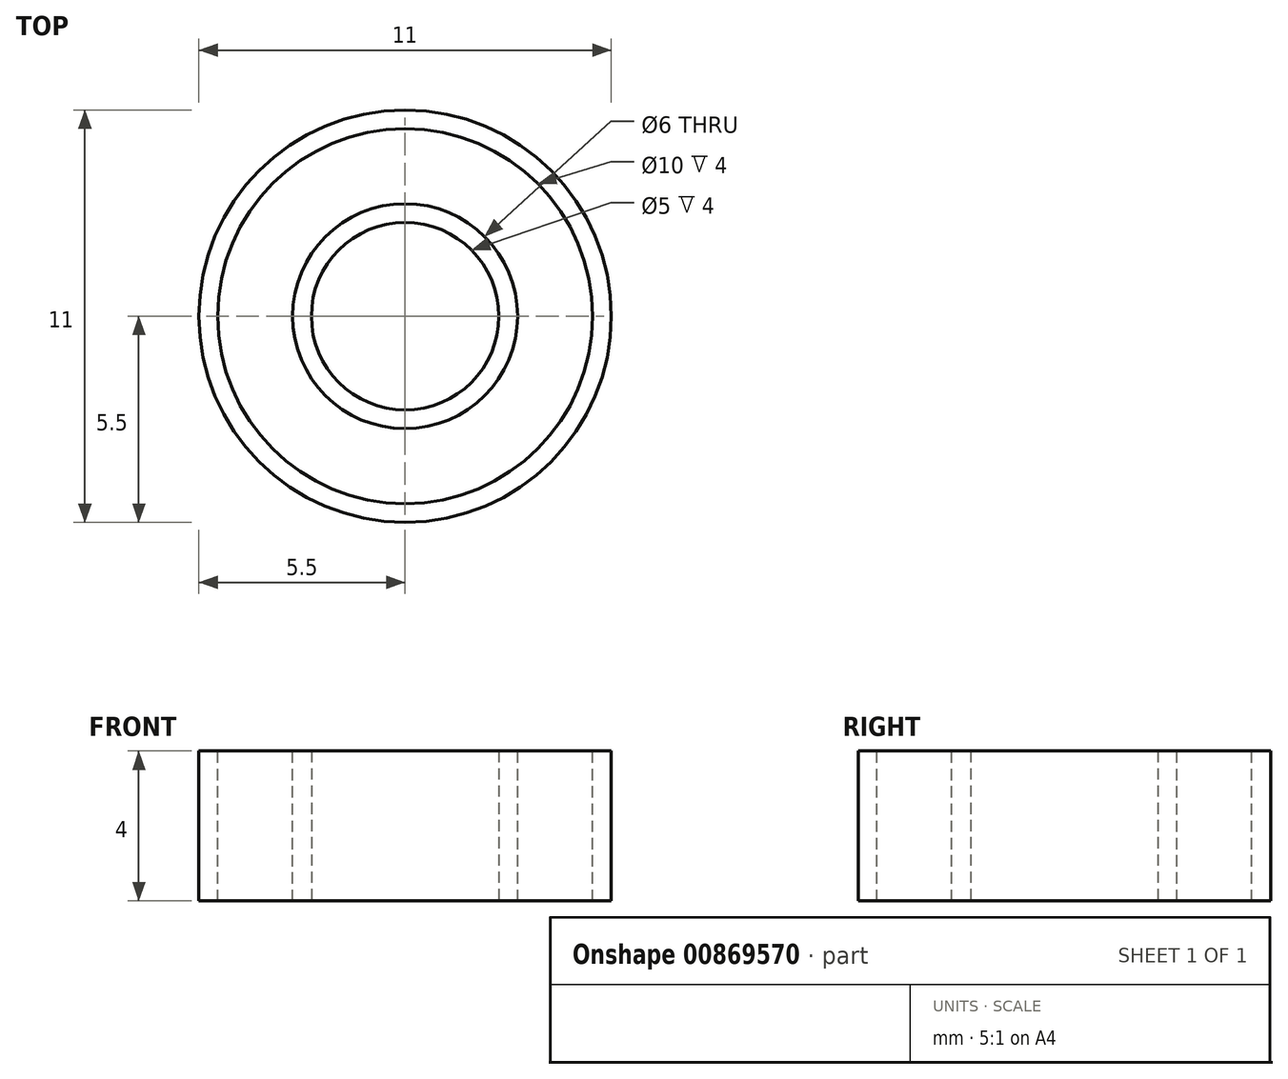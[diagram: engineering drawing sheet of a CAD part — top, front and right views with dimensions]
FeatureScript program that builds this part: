
annotation { "Feature Type Name" : "Feature", "Feature Type Description" : "" }
export const myFeature = defineFeature(function(context is Context, id is Id, definition is map)
    precondition{}
    {
        {
            var Q0;
            Q0=qCreatedBy(makeId("Top.planeOp"),FACE);
            var sketch = newSketch(context, id + "F0", { "sketchPlane" : qUnion([Q0])});
            skCircle(sketch, "E0", {"center": v(0, 0) * mm, "radius": 5.5 * mm});
            skCircle(sketch, "E1", {"center": v(0, 0) * mm, "radius": 2.5 * mm});
            skSolve(sketch);
        }
        {
            var Q0;
            Q0=makeQuery(id+"F0.imprint","IMPRINT",FACE,{"disambiguationData":[TD([[makeQuery(id+"F0.imprint","IMPRINT",EDGE,{"derivedFrom":sQuery(id+"F0.wireOp",EDGE,"E0")}),1.0]])]});
            extrude(context, id + "F1", {"entities" : qUnion([Q0]), "depth" : 4 * mm, "offsetDistance" : 25 * mm});
        }
        {
            var Q0;
            Q0=makeQuery(id+"F1.opExtrude","CAP_FACE",FACE,{"disambiguationData":[OSD([sQuery(id+"F0.wireOp",EDGE,"E0"),sQuery(id+"F0.wireOp",EDGE,"E1")])],"isStart":false});
            var sketch = newSketch(context, id + "F2", { "sketchPlane" : qUnion([Q0])});
            skCircle(sketch, "E2", {"center": v(0, 0) * mm, "radius": 3 * mm});
            skCircle(sketch, "E3", {"center": v(0, 0) * mm, "radius": 5 * mm});
            skSolve(sketch);
        }
        {
            var Q0;
            Q0 = qSketchRegion(id + "F2", true);
            extrude(context, id + "F3", {"entities" : qUnion([Q0]), "operationType" : NewBodyOperationType.REMOVE, "endBound" : BoundingType.THROUGH_ALL, "oppositeDirection" : true, "depth" : 25 * mm, "offsetDistance" : 25 * mm});
        }
        {
            var Q0;
            {var subQ0=sQuery(id+"F0.wireOp",EDGE,"E0");Q0=makeQuery(id+"F3.boolean.opBoolean","SPLIT",FACE,{"disambiguationData":[TD([makeQuery(id+"F1.opExtrude","SWEPT_FACE",FACE,{"disambiguationData":[OSD([subQ0])]})])],"derivedFrom":makeQuery(id+"F1.opExtrude","CAP_FACE",FACE,{"disambiguationData":[OSD([subQ0,sQuery(id+"F0.wireOp",EDGE,"E1")])],"isStart":false})});}
            var sketch = newSketch(context, id + "F4", { "sketchPlane" : qUnion([Q0])});
            skCircle(sketch, "E4", {"center": v(0, 0) * mm, "radius": 3 * mm});
            skCircle(sketch, "E5", {"center": v(0, 0) * mm, "radius": 5 * mm});
            skSolve(sketch);
        }
        {
            var Q0;
            Q0 = qSketchRegion(id + "F4", true);
            extrude(context, id + "F5", {"entities" : qUnion([Q0]), "oppositeDirection" : true, "depth" : 4 * mm, "offsetDistance" : 25 * mm});
        }
    });
